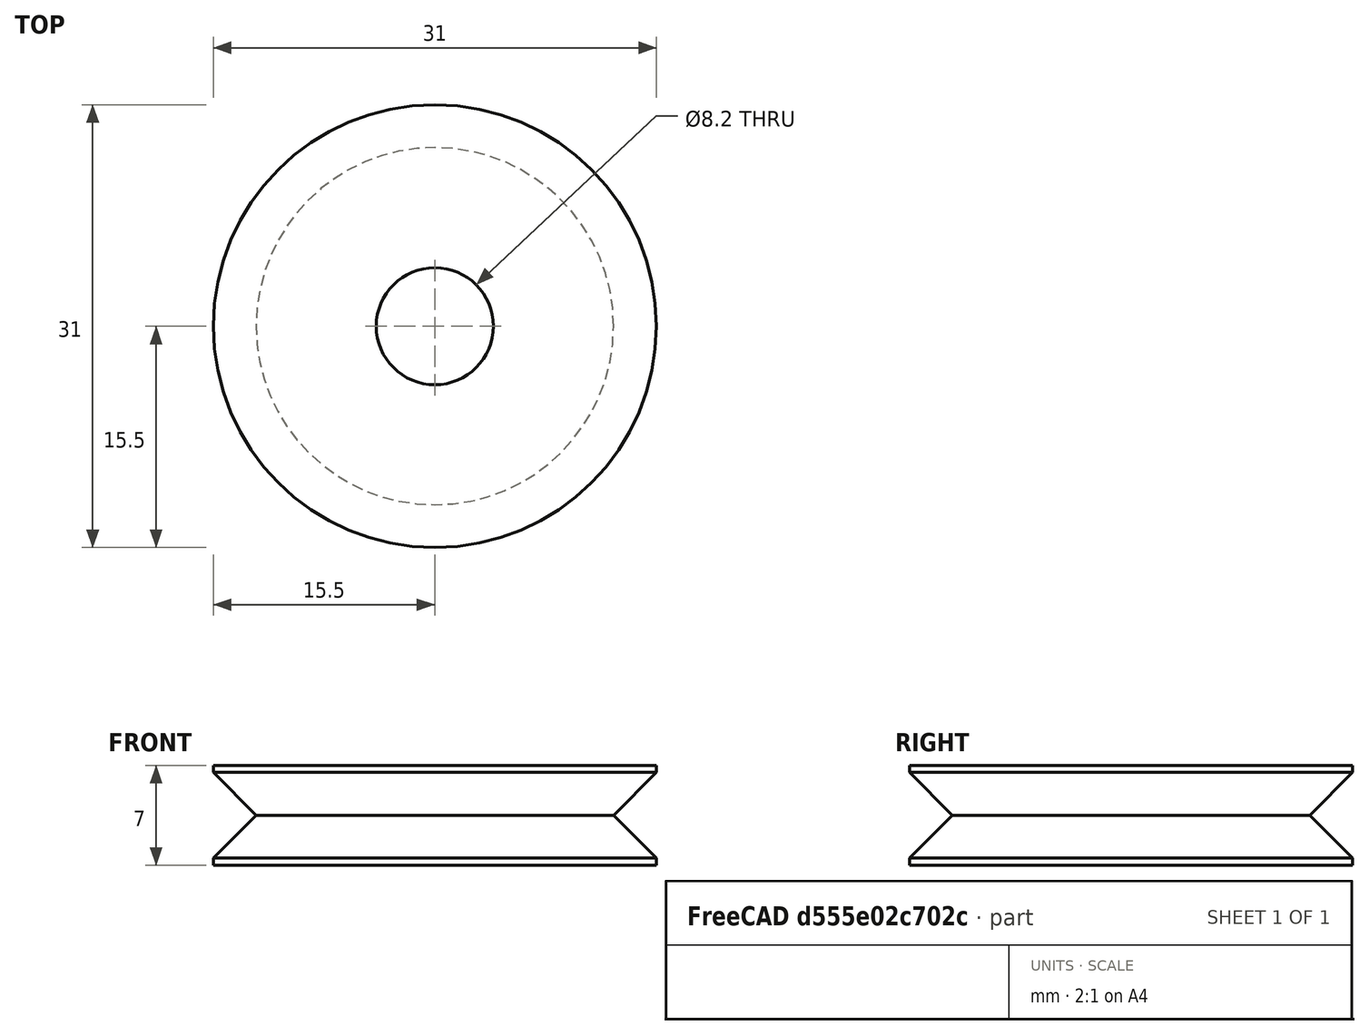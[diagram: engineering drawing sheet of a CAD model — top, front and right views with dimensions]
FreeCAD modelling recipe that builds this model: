
FCSTD DOCUMENT  (FreeCAD 0.20R27319 (Git))
Label: GroovedRingWithoutBearing
License: All rights reserved
LicenseURL: http://en.wikipedia.org/wiki/All_rights_reserved
objects: Sketcher::SketchObject×1, PartDesign::Revolution×1, PartDesign::Body×1, Spreadsheet::Sheet×1
note: 4 computed .brp shape members not serialized (recipe doc carries the construction recipe); baked Part::Feature solids carry a one-line shape summary decoded from their .brp

FEATURE [Sketcher::SketchObject] Sketch
  FullyConstrained = true
  MapMode = 5
  Placement = pos=(0,0,0) rot=(1,0,0;1.5708rad)
  Support = -> [XZ_Plane]
  expr: Constraints[17] = Spreadsheet.PulleyInnerDiameter / 2
  expr: Constraints[22] = Spreadsheet.PulleyOuterDiameter / 2
  expr: Constraints[6] = (Spreadsheet.BearingInnerDiameter + 0.2) / 2
  sketch-geometry (9):
    g0: LineSegment StartX=4.1 StartY=3.5 StartZ=0 EndX=15.5 EndY=3.5 EndZ=0
    g1: LineSegment StartX=4.1 StartY=3.5 StartZ=0 EndX=4.1 EndY=-3.5 EndZ=0
    g2: LineSegment StartX=4.1 StartY=-3.5 StartZ=0 EndX=15.5 EndY=-3.5 EndZ=0
    g3: LineSegment StartX=15.5 StartY=3.5 StartZ=0 EndX=15.5 EndY=3 EndZ=0
    g4: ArcOfCircle CenterX=15.5 CenterY=0 CenterZ=0 NormalX=0 NormalY=0 NormalZ=1 AngleXU=0 Radius=3 StartAngle=1.5708 EndAngle=4.71239
    g5: LineSegment StartX=15.5 StartY=-3 StartZ=0 EndX=15.5 EndY=-3.5 EndZ=0
    g6: GeomPoint X=12.5 Y=0 Z=0
    g7: LineSegment StartX=15.5 StartY=3 StartZ=0 EndX=12.5 EndY=0 EndZ=0
    g8: LineSegment StartX=12.5 StartY=0 StartZ=0 EndX=15.5 EndY=-3 EndZ=0
  constraints (23):
    c: Horizontal(g0)
    c: Coincident(g0,g1)
    c: Coincident(g1,g2)
    c: Horizontal(g2)
    c: Symmetric(g0,g1,g-1)
    c: DistanceY(g1,g1) = 7
    c: DistanceX(g-1,g0) = 4.1
    c: Vertical(g0,g2)
    c: Coincident(g3,g0)
    c: Coincident(g5,g2)
    c: PointOnObject(g4,g-1)
    c: Perpendicular(g5,g4) = 1.5708
    c: Coincident(g3,g4)
    c: Vertical(g3)
    c: Vertical(g5)
    c: PointOnObject(g6,g4)
    c: PointOnObject(g6,g-1)
    c: DistanceX(g-1,g6) = 12.5
    c: Coincident(g7,g3)
    c: Coincident(g7,g6)
    c: Coincident(g8,g6)
    c: Coincident(g8,g5)
    c: DistanceX(g-1,g0) = 15.5
FEATURE [PartDesign::Revolution] Revolution
  Angle = 360
  Axis = (0,-2e-16,1)
  Base = (0,0,0)
  Placement = pos=(0,0,0) rot=(1,0,0;1.5708rad)
  Profile = -> Sketch
  ReferenceAxis = -> Sketch [V_Axis]
  Reversed = true
FEATURE [PartDesign::Body] Body
  Group = -> [Sketch,Revolution]
  Origin = -> Origin
  Tip = -> Revolution
FEATURE [Spreadsheet::Sheet] Spreadsheet
  cells = A1=Pulley Outer Diameter; B1(PulleyOuterDiameter)==B2 + 6; A2=Pulley Inner Diameter; B2(PulleyInnerDiameter)=25; A3=Pulley Clearance; B3(PulleyClearance)=1; A4=Pulley Centre Diameter; B4(PulleyCentreDiameter)=8; A5=Pulley Thickness; B5(PulleyThickness)=7; A6=Bearing Outer Diameter; B6(BearingOuterDiameter)=22; A7=Bearing Inner Diameter; B7(BearingInnerDiameter)=8
